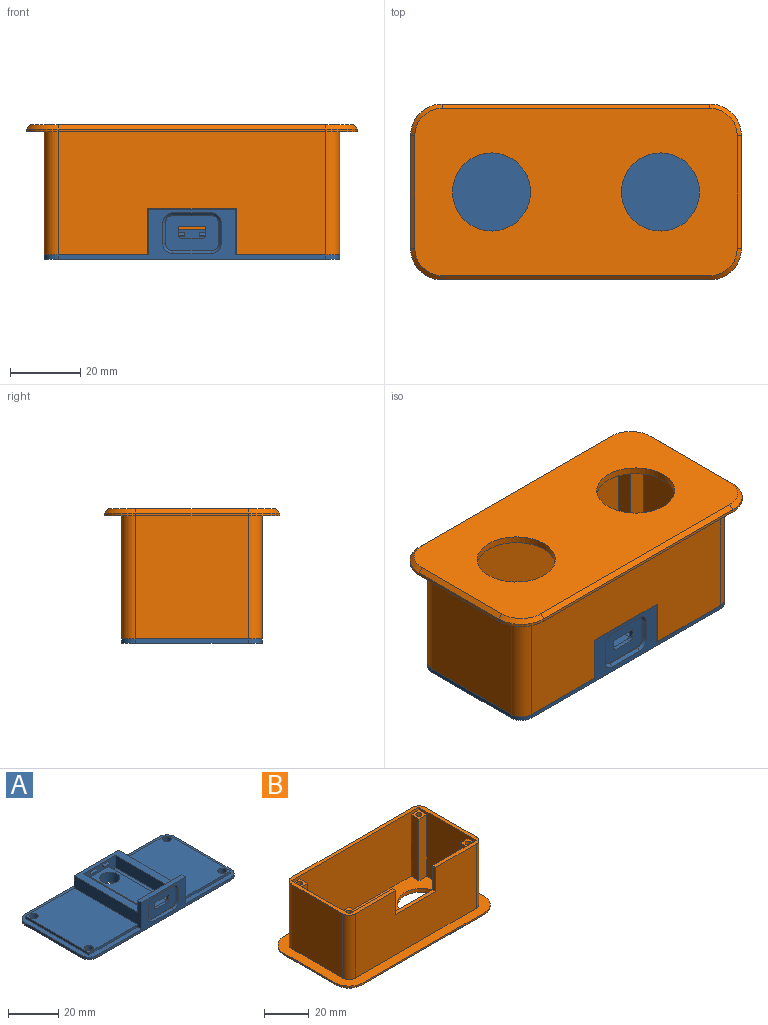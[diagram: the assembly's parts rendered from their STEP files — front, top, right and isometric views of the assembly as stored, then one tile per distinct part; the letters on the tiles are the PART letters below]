
ASSEMBLY  parts=2 mates=1
PART A: 68 faces, bbox 84x40x14.2 mm
  f0: plane 3.6x1.2mm, normal (1,0,0), area 3.6mm2, adj f1,f5,f6,f36
  f1: cylinder r=1mm len=1.2mm, axis (0,-1,0), area 1.9mm2, adj f0,f2,f6,f36
  f2: plane 5.8x1.2mm, normal (0,0,1), area 7mm2, adj f1,f3,f6,f36
  f3: cylinder r=1mm len=1.2mm, axis (0,-1,0), area 1.9mm2, adj f2,f4,f6,f36
  f4: plane 3.6x1.2mm, normal (-1,0,0), area 3.6mm2, adj f3,f5,f6,f36
  f5: plane 7.8x1.2mm, normal (0,0.71,-0.71), area 13.2mm2, adj f0,f4,f6,f36
  f6: plane 25x11.8mm, normal (0,1,0), area 193.2mm2, adj f0,f1,f2,f3,f4,f5,f8,f9
  f7: plane 76x14.2mm, normal (0,-1,0), area 230.4mm2, adj f11,f18,f19,f20,f26,f27,f28,f45
  f8: plane 34x4mm, normal (0,0,1), area 136mm2, adj f6,f29,f31,f34
  f9: plane 34x4mm, normal (0,0,1), area 136mm2, adj f6,f30,f31,f33
  f10: plane 35.6x27.3mm, normal (0,0,1), area 953.7mm2, adj f22,f23,f25,f27,f55,f56
  f11: plane 84x40mm, normal (0,0,1), area 457.5mm2, adj f7,f12,f13,f14,f15,f16,f17,f18
  f12: plane 27.3x1.2mm, normal (0,-1,0), area 32.8mm2, adj f11,f21,f24,f26
  f13: plane 32x1.2mm, normal (1,0,0), area 38.4mm2, adj f11,f14,f19,f20
  f14: cylinder r=4mm len=4mm, axis (0,0,-1), area 7.5mm2, adj f11,f13,f15,f20
  f15: plane 76x1.2mm, normal (0,1,0), area 91.2mm2, adj f11,f14,f16,f20
  f16: cylinder r=4mm len=4mm, axis (0,0,-1), area 7.5mm2, adj f11,f15,f17,f20
  f17: plane 32x1.2mm, normal (-1,0,0), area 38.4mm2, adj f11,f16,f18,f20
  f18: cylinder r=4mm len=4mm, axis (0,0,-1), area 7.5mm2, adj f7,f11,f17,f20
  f19: cylinder r=4mm len=4mm, axis (0,0,-1), area 7.5mm2, adj f7,f11,f13,f20
  f20: plane 84x40mm, normal (0,0,-1), area 3259.7mm2, adj f7,f13,f14,f15,f16,f17,f18,f19
  f21: plane 35.6x27.3mm, normal (0,0,1), area 953.7mm2, adj f12,f24,f25,f26,f53,f54
  f22: plane 35.6x1.2mm, normal (-1,0,0), area 42.7mm2, adj f10,f11,f23,f25
  f23: plane 27.3x1.2mm, normal (0,-1,0), area 32.8mm2, adj f10,f11,f22,f27
  f24: plane 35.6x1.2mm, normal (1,0,0), area 42.7mm2, adj f11,f12,f21,f25
  f25: plane 79.6x7.2mm, normal (0,1,0), area 245.5mm2, adj f10,f11,f21,f22,f24,f26,f27,f32
  f26: plane 37.8x13mm, normal (1,0,0), area 242.2mm2, adj f6,f7,f11,f12,f21,f25,f28,f32
  f27: plane 37.8x13mm, normal (-1,0,0), area 242.2mm2, adj f6,f7,f10,f11,f23,f25,f28,f32
  f28: plane 25x2.2mm, normal (0,0,1), area 55mm2, adj f6,f7,f26,f27
  f29: plane 34x6mm, normal (-1,0,0), area 204mm2, adj f6,f8,f31,f32
  f30: plane 34x6mm, normal (1,0,0), area 204mm2, adj f6,f9,f31,f32
  f31: plane 18.2x6mm, normal (0,-1,0), area 77.7mm2, adj f8,f9,f29,f30,f32,f33,f34,f35
  f32: plane 35.6x25mm, normal (0,0,1), area 271.2mm2, adj f6,f25,f26,f27,f29,f30,f31
  f33: plane 34x2.5mm, normal (-1,0,0), area 85mm2, adj f6,f9,f31,f35
  f34: plane 34x2.5mm, normal (1,0,0), area 85mm2, adj f6,f8,f31,f35
  f35: plane 34x10.2mm, normal (0,0,1), area 296.5mm2, adj f6,f31,f33,f34,f67
  f36: plane 15x10mm, normal (0,-1,0), area 120.5mm2, adj f0,f1,f2,f3,f4,f5,f37,f38
  f37: plane 6x0.2mm, normal (-1,0,0), area 1.2mm2, adj f36,f38,f44,f48
  f38: cylinder r=2mm len=2mm, axis (0,-1,0), area 0.6mm2, adj f36,f37,f39,f50
  f39: plane 11x0.2mm, normal (0,0,-1), area 2.2mm2, adj f36,f38,f40,f52
  f40: cylinder r=2mm len=2mm, axis (0,-1,0), area 0.6mm2, adj f36,f39,f41,f51
  f41: plane 6x0.2mm, normal (1,0,0), area 1.2mm2, adj f36,f40,f42,f49
  f42: cylinder r=2mm len=2mm, axis (0,-1,0), area 0.6mm2, adj f36,f41,f43,f47
  f43: plane 11x0.2mm, normal (0,0,1), area 2.2mm2, adj f36,f42,f44,f45
  f44: cylinder r=2mm len=2mm, axis (0,-1,0), area 0.6mm2, adj f36,f37,f43,f46
  f45: plane 11x0.8mm, normal (0,-0.71,0.71), area 12.4mm2, adj f7,f43,f46,f47
  f46: cone r=2mm half-angle=45deg, axis (0,-1,0), area 4.3mm2, adj f7,f44,f45,f48
  f47: cone r=2mm half-angle=45deg, axis (0,-1,0), area 4.3mm2, adj f7,f42,f45,f49
  f48: plane 6x0.8mm, normal (-0.71,-0.71,0), area 6.8mm2, adj f7,f37,f46,f50
  f49: plane 6x0.8mm, normal (0.71,-0.71,0), area 6.8mm2, adj f7,f41,f47,f51
  f50: cone r=2mm half-angle=45deg, axis (0,-1,0), area 4.3mm2, adj f7,f38,f48,f52
  f51: cone r=2mm half-angle=45deg, axis (0,-1,0), area 4.3mm2, adj f7,f40,f49,f52
  f52: plane 11x0.8mm, normal (0,-0.71,-0.71), area 12.4mm2, adj f7,f39,f50,f51
  f53: cylinder r=1.7mm len=3.4mm, axis (0,0,1), area 25.6mm2, adj f20,f21
  f54: cylinder r=1.7mm len=3.4mm, axis (0,0,1), area 25.6mm2, adj f20,f21
  f55: cylinder r=1.7mm len=3.4mm, axis (0,0,1), area 25.6mm2, adj f10,f20
  f56: cylinder r=1.7mm len=3.4mm, axis (0,0,1), area 25.6mm2, adj f10,f20
  f57: plane 3x0.8mm, normal (0,0,-1), area 2.4mm2, adj f31,f58,f59,f60
  f58: plane 1x0.8mm, normal (1,0,0), area 0.5mm2, adj f31,f57,f60,f66
  f59: plane 1x0.8mm, normal (-1,0,0), area 0.5mm2, adj f31,f57,f60,f66
  f60: plane 3x0.2mm, normal (0,-1,0), area 0.6mm2, adj f57,f58,f59,f66
  f61: plane 1x0.8mm, normal (-1,0,0), area 0.5mm2, adj f31,f62,f64,f65
  f62: plane 3x0.8mm, normal (0,0,-1), area 2.4mm2, adj f31,f61,f63,f64
  f63: plane 1x0.8mm, normal (1,0,0), area 0.5mm2, adj f31,f62,f64,f65
  f64: plane 3x0.2mm, normal (0,-1,0), area 0.6mm2, adj f61,f62,f63,f65
  f65: plane 3x0.8mm, normal (0,-0.71,0.71), area 3.4mm2, adj f31,f61,f63,f64
  f66: plane 3x0.8mm, normal (0,-0.71,0.71), area 3.4mm2, adj f31,f58,f59,f60
  f67: cylinder r=4mm len=8mm, axis (0,0,1), area 123.2mm2, adj f20,f35
PART B: 57 faces, bbox 94x50x37 mm
  f0: plane 36x35mm, normal (-1,0,0), area 924mm2, adj f1,f3,f4,f26,f40,f42,f46,f47
  f1: plane 80x36mm, normal (0,0,1), area 2005.8mm2, adj f0,f2,f3,f4,f16,f17,f38,f39
  f2: plane 36x35mm, normal (1,0,0), area 924mm2, adj f1,f3,f4,f26,f37,f38,f43,f44
  f3: plane 80x35mm, normal (0,-1,0), area 2464mm2, adj f0,f1,f2,f26,f43,f45,f46,f48
  f4: plane 80x35mm, normal (0,1,0), area 2131.4mm2, adj f0,f1,f2,f26,f34,f35,f36,f37
  f5: plane 76x35mm, normal (0,-1,0), area 2327.4mm2, adj f14,f26,f32,f33,f34,f35,f36
  f6: plane 32x0.8mm, normal (-1,0,0), area 25.6mm2, adj f7,f13,f14,f22
  f7: cylinder r=9mm len=9mm, axis (0,0,-1), area 11.3mm2, adj f6,f8,f14,f20
  f8: plane 76x0.8mm, normal (0,-1,0), area 60.8mm2, adj f7,f9,f14,f18
  f9: cylinder r=9mm len=9mm, axis (0,0,-1), area 11.3mm2, adj f8,f10,f14,f19
  f10: plane 32x0.8mm, normal (1,0,0), area 25.6mm2, adj f9,f11,f14,f21
  f11: cylinder r=9mm len=9mm, axis (0,0,-1), area 11.3mm2, adj f10,f12,f14,f23
  f12: plane 76x0.8mm, normal (0,1,0), area 60.8mm2, adj f11,f13,f14,f25
  f13: cylinder r=9mm len=9mm, axis (0,0,-1), area 11.3mm2, adj f6,f12,f14,f24
  f14: plane 94x50mm, normal (0,0,1), area 1284.2mm2, adj f5,f6,f7,f8,f9,f10,f11,f12
  f15: plane 91.6x47.6mm, normal (0,0,-1), area 3533.8mm2, adj f16,f17,f18,f19,f20,f21,f22,f23
  f16: cylinder r=11.1mm len=22.2mm, axis (0,0,-1), area 139.5mm2, adj f1,f15
  f17: cylinder r=11.1mm len=22.2mm, axis (0,0,-1), area 139.5mm2, adj f1,f15
  f18: plane 76x1.2mm, normal (0,-0.71,-0.71), area 129mm2, adj f8,f15,f19,f20
  f19: cone r=9mm half-angle=45deg, axis (0,0,1), area 22.4mm2, adj f9,f15,f18,f21
  f20: cone r=9mm half-angle=45deg, axis (0,0,1), area 22.4mm2, adj f7,f15,f18,f22
  f21: plane 32x1.2mm, normal (0.71,0,-0.71), area 54.3mm2, adj f10,f15,f19,f23
  f22: plane 32x1.2mm, normal (-0.71,0,-0.71), area 54.3mm2, adj f6,f15,f20,f24
  f23: cone r=9mm half-angle=45deg, axis (0,0,1), area 22.4mm2, adj f11,f15,f21,f25
  f24: cone r=9mm half-angle=45deg, axis (0,0,1), area 22.4mm2, adj f13,f15,f22,f25
  f25: plane 76x1.2mm, normal (0,0.71,-0.71), area 129mm2, adj f12,f15,f23,f24
  f26: plane 84x40mm, normal (0,0,1), area 415.9mm2, adj f0,f2,f3,f4,f5,f27,f28,f29
  f27: plane 35x32mm, normal (1,0,0), area 1120mm2, adj f14,f26,f28,f33
  f28: cylinder r=4mm len=35mm, axis (0,0,-1), area 219.9mm2, adj f14,f26,f27,f29
  f29: plane 76x35mm, normal (0,1,0), area 2660mm2, adj f14,f26,f28,f30
  f30: cylinder r=4mm len=35mm, axis (0,0,-1), area 219.9mm2, adj f14,f26,f29,f31
  f31: plane 35x32mm, normal (-1,0,0), area 1120mm2, adj f14,f26,f30,f32
  f32: cylinder r=4mm len=35mm, axis (0,0,-1), area 219.9mm2, adj f5,f14,f26,f31
  f33: cylinder r=4mm len=35mm, axis (0,0,-1), area 219.9mm2, adj f5,f14,f26,f27
  f34: plane 13.2x2mm, normal (1,0,0), area 26.4mm2, adj f4,f5,f26,f36
  f35: plane 13.2x2mm, normal (-1,0,0), area 26.4mm2, adj f4,f5,f26,f36
  f36: plane 25.2x2mm, normal (0,0,1), area 50.4mm2, adj f4,f5,f34,f35
  f37: plane 5x5mm, normal (0,0,1), area 19.3mm2, adj f2,f4,f38,f39,f55
  f38: plane 33.6x5mm, normal (0,1,0), area 168mm2, adj f1,f2,f37,f39
  f39: plane 33.6x5mm, normal (1,0,0), area 168mm2, adj f1,f4,f37,f38
  f40: plane 5x5mm, normal (0,0,1), area 19.3mm2, adj f0,f4,f41,f42,f53
  f41: plane 33.6x5mm, normal (-1,0,0), area 168mm2, adj f1,f4,f40,f42
  f42: plane 33.6x5mm, normal (0,1,0), area 168mm2, adj f0,f1,f40,f41
  f43: plane 5x5mm, normal (0,0,1), area 19.3mm2, adj f2,f3,f44,f45,f51
  f44: plane 33.6x5mm, normal (0,-1,0), area 168mm2, adj f1,f2,f43,f45
  f45: plane 33.6x5mm, normal (1,0,0), area 168mm2, adj f1,f3,f43,f44
  f46: plane 5x5mm, normal (0,0,1), area 19.3mm2, adj f0,f3,f47,f48,f49
  f47: plane 33.6x5mm, normal (0,-1,0), area 168mm2, adj f0,f1,f46,f48
  f48: plane 33.6x5mm, normal (-1,0,0), area 168mm2, adj f1,f3,f46,f47
  f49: cylinder r=1.35mm len=25mm, axis (0,0,1), area 212.1mm2, adj f46,f50
  f50: plane 2.7x2.7mm, normal (0,0,1), area 5.7mm2, adj f49
  f51: cylinder r=1.35mm len=25mm, axis (0,0,1), area 212.1mm2, adj f43,f52
  f52: plane 2.7x2.7mm, normal (0,0,1), area 5.7mm2, adj f51
  f53: cylinder r=1.35mm len=25mm, axis (0,0,1), area 212.1mm2, adj f40,f54
  f54: plane 2.7x2.7mm, normal (0,0,1), area 5.7mm2, adj f53
  f55: cylinder r=1.35mm len=25mm, axis (0,0,1), area 212.1mm2, adj f37,f56
  f56: plane 2.7x2.7mm, normal (0,0,1), area 5.7mm2, adj f55
PLACE A t=(3.28,-4.05,9.77)mm
PLACE B rot(axis=(0,1,0),180deg) t=(3.28,-4.08,47.97)mm
MATE fastened B.f26 <-> A.f11  axis (0,0,-1) through (3.28,-1.78,10.97)mm
